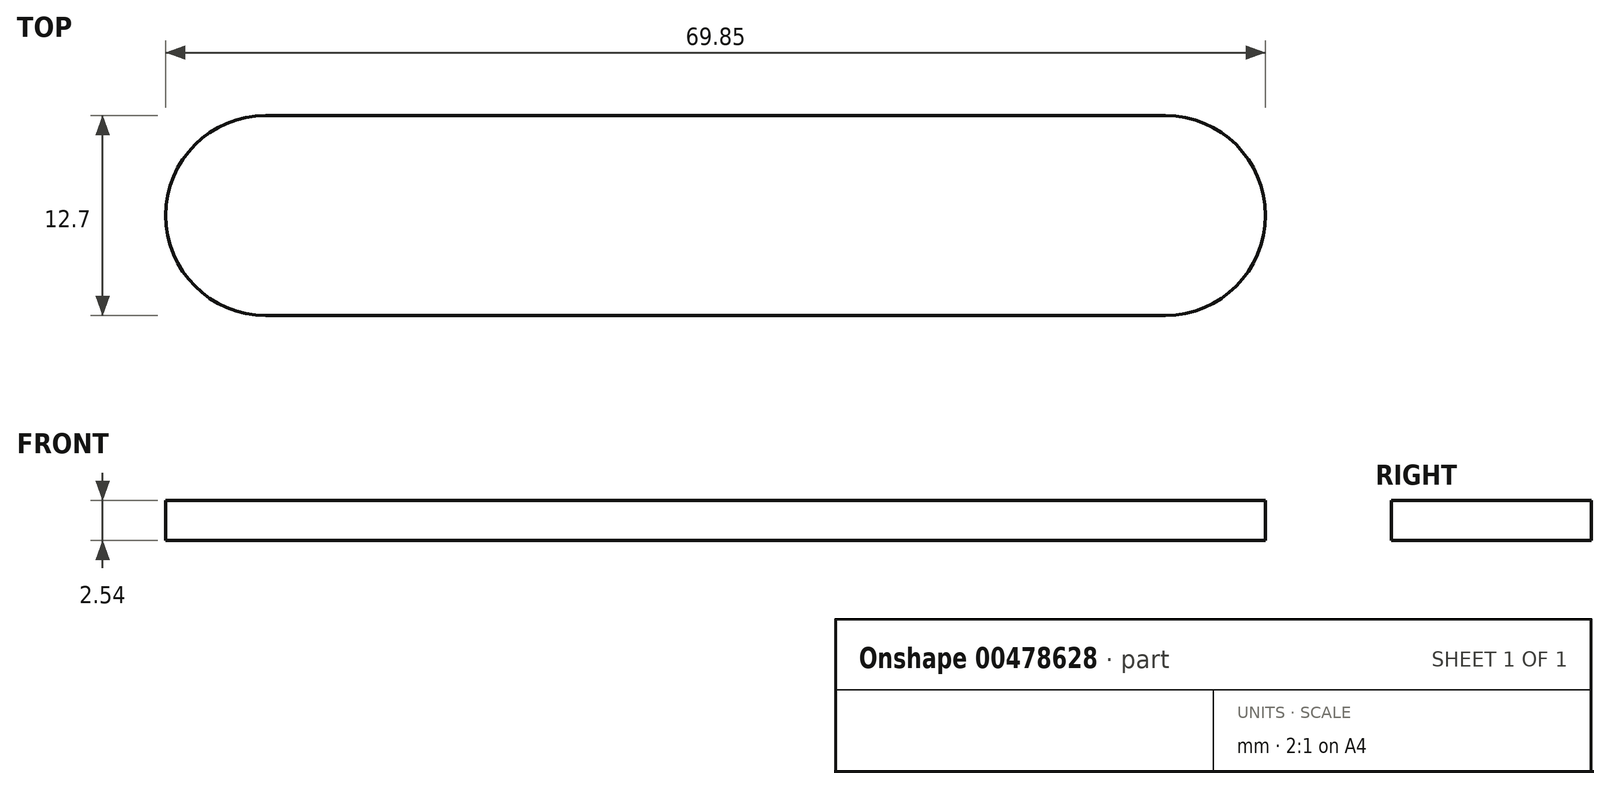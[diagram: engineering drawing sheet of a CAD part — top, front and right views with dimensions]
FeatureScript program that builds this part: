
annotation { "Feature Type Name" : "Feature", "Feature Type Description" : "" }
export const myFeature = defineFeature(function(context is Context, id is Id, definition is map)
    precondition{}
    {
        {
            var Q0;
            Q0=qCreatedBy(makeId("Top.planeOp"),FACE);
            var sketch = newSketch(context, id + "F0", { "sketchPlane" : qUnion([Q0])});
            skLineSegment(sketch, "E0.bottom", {"start": v(-15.55, -2.83) * mm, "end": v(41.6, -2.83) * mm});
            skLineSegment(sketch, "E0.top", {"start": v(-15.55, -15.53) * mm, "end": v(41.6, -15.53) * mm});
            skLineSegment(sketch, "E0.left", {"start": v(-21.9, -9.18) * mm, "end": v(-21.9, -9.18) * mm});
            skLineSegment(sketch, "E0.right", {"start": v(47.95, -9.18) * mm, "end": v(47.95, -9.18) * mm});
            skPoint(sketch, "E1.visualSharp", {"position": v(-21.9, -2.83) * mm});
            skArc(sketch, "E1.filletArc", {"start": v(-15.55, -2.83) * mm, "mid": v(-20.04, -4.69) * mm, "end": v(-21.9, -9.18) * mm});
            skPoint(sketch, "E2.visualSharp", {"position": v(-21.9, -15.53) * mm});
            skArc(sketch, "E2.filletArc", {"start": v(-21.9, -9.18) * mm, "mid": v(-20.04, -13.67) * mm, "end": v(-15.55, -15.53) * mm});
            skPoint(sketch, "E3.visualSharp", {"position": v(47.95, -2.83) * mm});
            skArc(sketch, "E3.filletArc", {"start": v(47.95, -9.18) * mm, "mid": v(46.1, -4.69) * mm, "end": v(41.6, -2.83) * mm});
            skPoint(sketch, "E4.visualSharp", {"position": v(47.95, -15.53) * mm});
            skArc(sketch, "E4.filletArc", {"start": v(41.6, -15.53) * mm, "mid": v(46.1, -13.67) * mm, "end": v(47.95, -9.18) * mm});
            skSolve(sketch);
        }
        {
            var Q0;
            Q0=makeQuery(id+"F0.imprint","IMPRINT",FACE,{"disambiguationData":[TD([[makeQuery(id+"F0.imprint","IMPRINT",EDGE,{"derivedFrom":sQuery(id+"F0.wireOp",EDGE,"E0.bottom")}),-1.0]])]});
            extrude(context, id + "F1", {"entities" : qUnion([Q0]), "oppositeDirection" : true, "depth" : 2.54 * mm});
        }
    });
